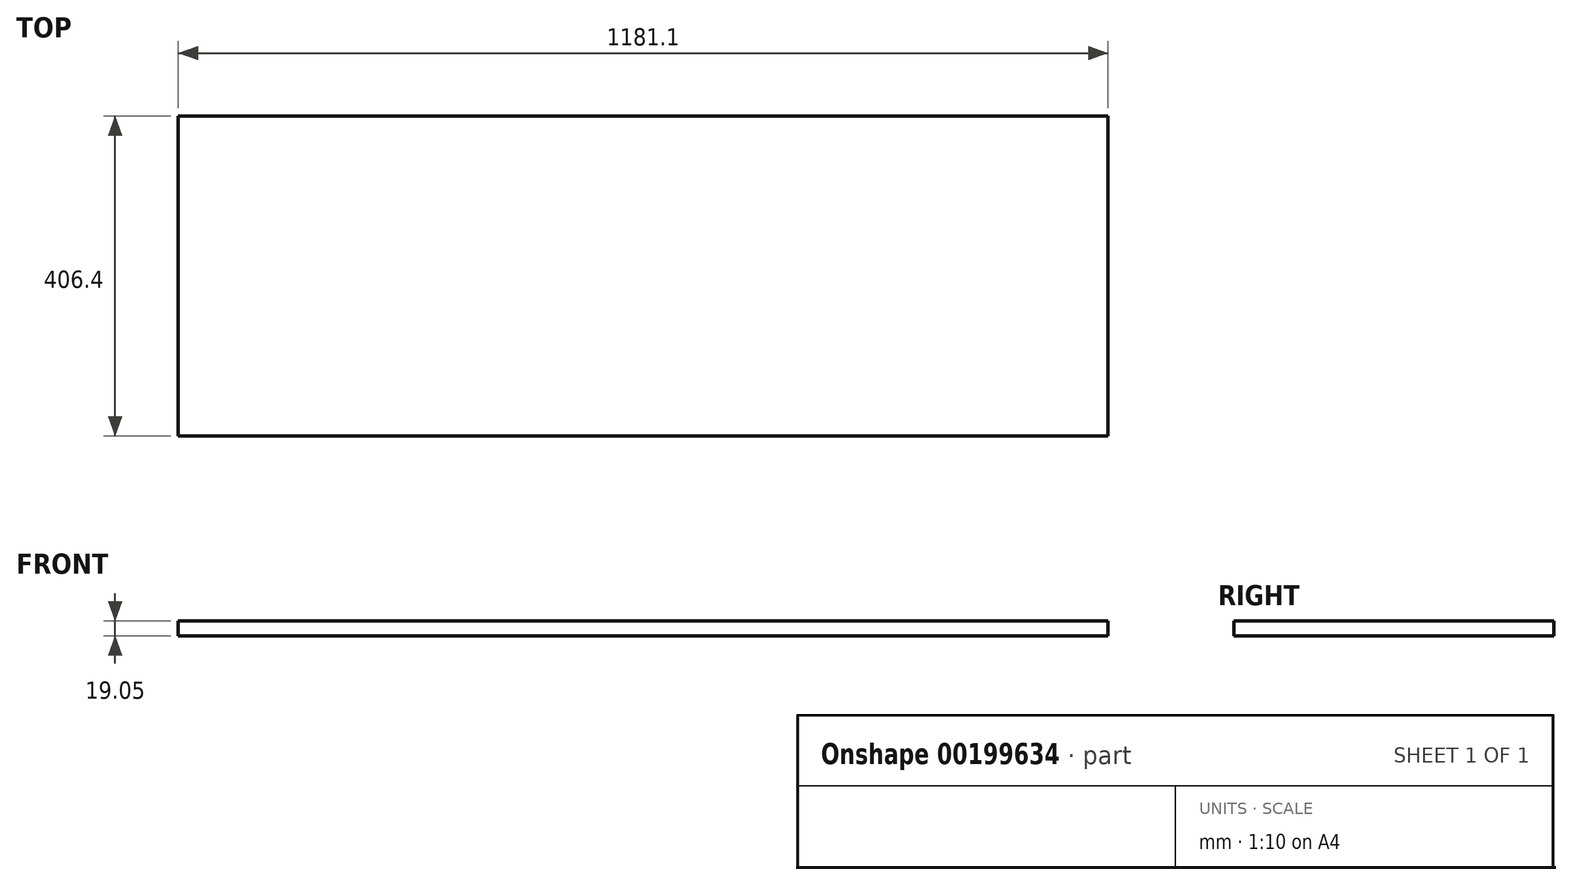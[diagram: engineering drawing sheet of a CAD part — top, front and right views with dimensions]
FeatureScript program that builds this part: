
annotation { "Feature Type Name" : "Feature", "Feature Type Description" : "" }
export const myFeature = defineFeature(function(context is Context, id is Id, definition is map)
    precondition{}
    {
        {
            var Q0;
            Q0=qCreatedBy(makeId("Top.planeOp"),FACE);
            var sketch = newSketch(context, id + "F0", { "sketchPlane" : qUnion([Q0])});
            skLineSegment(sketch, "E0.bottom", {"start": v(-606.37, 116.3) * mm, "end": v(574.73, 116.3) * mm});
            skLineSegment(sketch, "E0.top", {"start": v(-606.37, -290.1) * mm, "end": v(574.73, -290.1) * mm});
            skLineSegment(sketch, "E0.left", {"start": v(-606.37, 116.3) * mm, "end": v(-606.37, -290.1) * mm});
            skLineSegment(sketch, "E0.right", {"start": v(574.73, 116.3) * mm, "end": v(574.73, -290.1) * mm});
            skSolve(sketch);
        }
        {
            var Q0;
            Q0=makeQuery(id+"F0.imprint","IMPRINT",FACE,{"disambiguationData":[TD([[makeQuery(id+"F0.imprint","IMPRINT",EDGE,{"derivedFrom":sQuery(id+"F0.wireOp",EDGE,"E0.bottom")}),-1.0]])]});
            extrude(context, id + "F1", {"entities" : qUnion([Q0]), "depth" : 19.05 * mm});
        }
    });
